# Revit family: A_Window_Double Sliding
name_source: partatom
category: Windows
units: mm (PartAtom-declared; Revit-internal decimal feet)

## family parameters
Always vertical = Yes
Cut with Voids When Loaded = No
Host = Wall
OmniClass Number = 23.30.20.00
OmniClass Title = Windows
Room Calculation Point = No
Shared = No

## types (1)
- 1500Wx1500H
    Analytic Construction = <None>
    Default Sill Height = 800 mm  [stored 2.62467 ft]
    Define Thermal Properties by = Schematic Type
    Frame_Material = Paint - Sienna
    Frame_Offset = -25 mm  [stored -0.082021 ft]
    Frame_Thickness = 50 mm  [stored 0.164042 ft]
    Frame_Width = 100 mm  [stored 0.328084 ft]
    Glass_Material = 1. GL-B-01
    Glass_Thickness = 25 mm  [stored 0.082021 ft]
    Height = 1500 mm  [stored 4.92126 ft]
    Panel_Frame_Material = Paint - Sienna
    Panel_Frame_Width = 50 mm  [stored 0.164042 ft]
    Panel_Height = 1400 mm  [stored 4.59318 ft]
    Panel_Width = 725 mm  [stored 2.37861 ft]
    Wall Closure = By host
    Width = 1500 mm  [stored 4.92126 ft]

note: [stored X ft] marks values corroborated as IEEE doubles in the binary element streams (Revit-internal decimal feet)

## geometry (parser evidence)
native form markers: Blend x4, Sweep x5
no freeform markers — native parametric forms only
